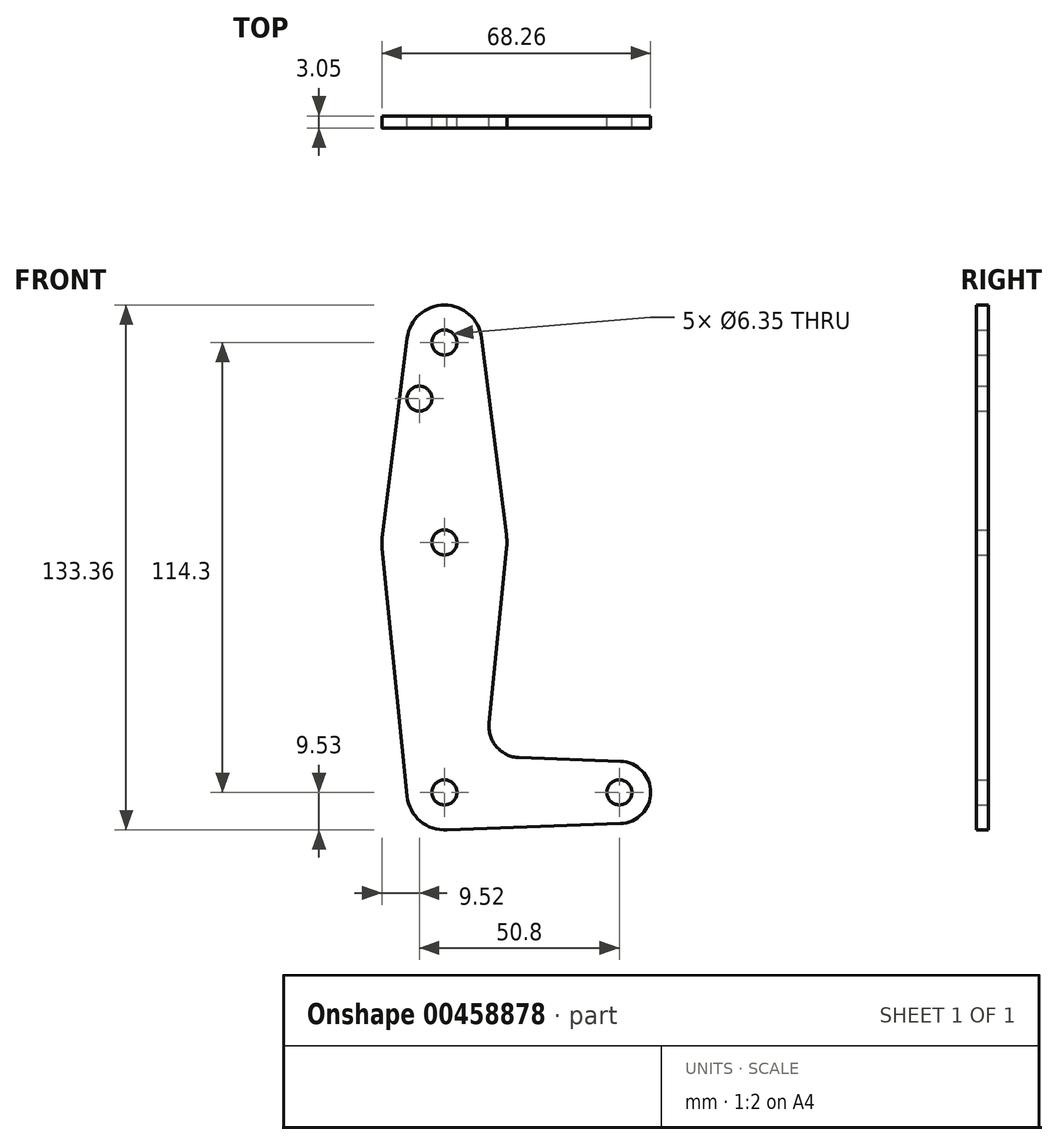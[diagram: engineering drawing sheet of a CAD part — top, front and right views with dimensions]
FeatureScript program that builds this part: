
annotation { "Feature Type Name" : "Feature", "Feature Type Description" : "" }
export const myFeature = defineFeature(function(context is Context, id is Id, definition is map)
    precondition{}
    {
        {
            var Q0;
            Q0=qCreatedBy(makeId("Front.planeOp"),FACE);
            var sketch = newSketch(context, id + "F0", { "sketchPlane" : qUnion([Q0])});
            skCircle(sketch, "E0", {"center": v(0, 0) * mm, "radius": 9.53 * mm});
            skCircle(sketch, "E1", {"center": v(0, 63.5) * mm, "radius": 15.88 * mm});
            skCircle(sketch, "E2", {"center": v(0, 114.3) * mm, "radius": 9.53 * mm});
            skCircle(sketch, "E3", {"center": v(44.45, 0) * mm, "radius": 7.94 * mm});
            skLineSegment(sketch, "E4", {"start": v(-9.45, 115.5) * mm, "end": v(-15.75, 65.48) * mm});
            skLineSegment(sketch, "E5", {"start": v(9.45, 115.5) * mm, "end": v(15.75, 65.48) * mm});
            skLineSegment(sketch, "E6", {"start": v(-15.8, 61.91) * mm, "end": v(-9.48, -0.95) * mm});
            skLineSegment(sketch, "E7", {"start": v(15.8, 61.91) * mm, "end": v(11.34, 17.59) * mm});
            skLineSegment(sketch, "E8", {"start": v(18.97, 8.85) * mm, "end": v(44.73, 7.93) * mm});
            skLineSegment(sketch, "E9", {"start": v(0, -9.53) * mm, "end": v(44.73, -7.93) * mm});
            skCircle(sketch, "E10", {"center": v(0, 114.3) * mm, "radius": 3.18 * mm});
            skCircle(sketch, "E11", {"center": v(0, 63.5) * mm, "radius": 3.18 * mm});
            skCircle(sketch, "E12", {"center": v(0, 0) * mm, "radius": 3.18 * mm});
            skCircle(sketch, "E13", {"center": v(44.45, 0) * mm, "radius": 3.18 * mm});
            skPoint(sketch, "E14.newPointA", {"position": v(0, 9.53) * mm});
            skArc(sketch, "E14.filletArc", {"start": v(11.34, 17.59) * mm, "mid": v(13.26, 11.57) * mm, "end": v(18.97, 8.85) * mm});
            skCircle(sketch, "E15.MirrorC", {"center": v(-6.35, 100.03) * mm, "radius": 3.18 * mm});
            skLineSegment(sketch, "E16", {"start": v(0, 114.3) * mm, "end": v(0, 0) * mm, "construction": true});
            skSolve(sketch);
        }
        {
            var Q0;
            Q0 = qSketchRegion(id + "F0", true);
            extrude(context, id + "F1", {"entities" : qUnion([Q0]), "depth" : 3.05 * mm});
        }
    });
